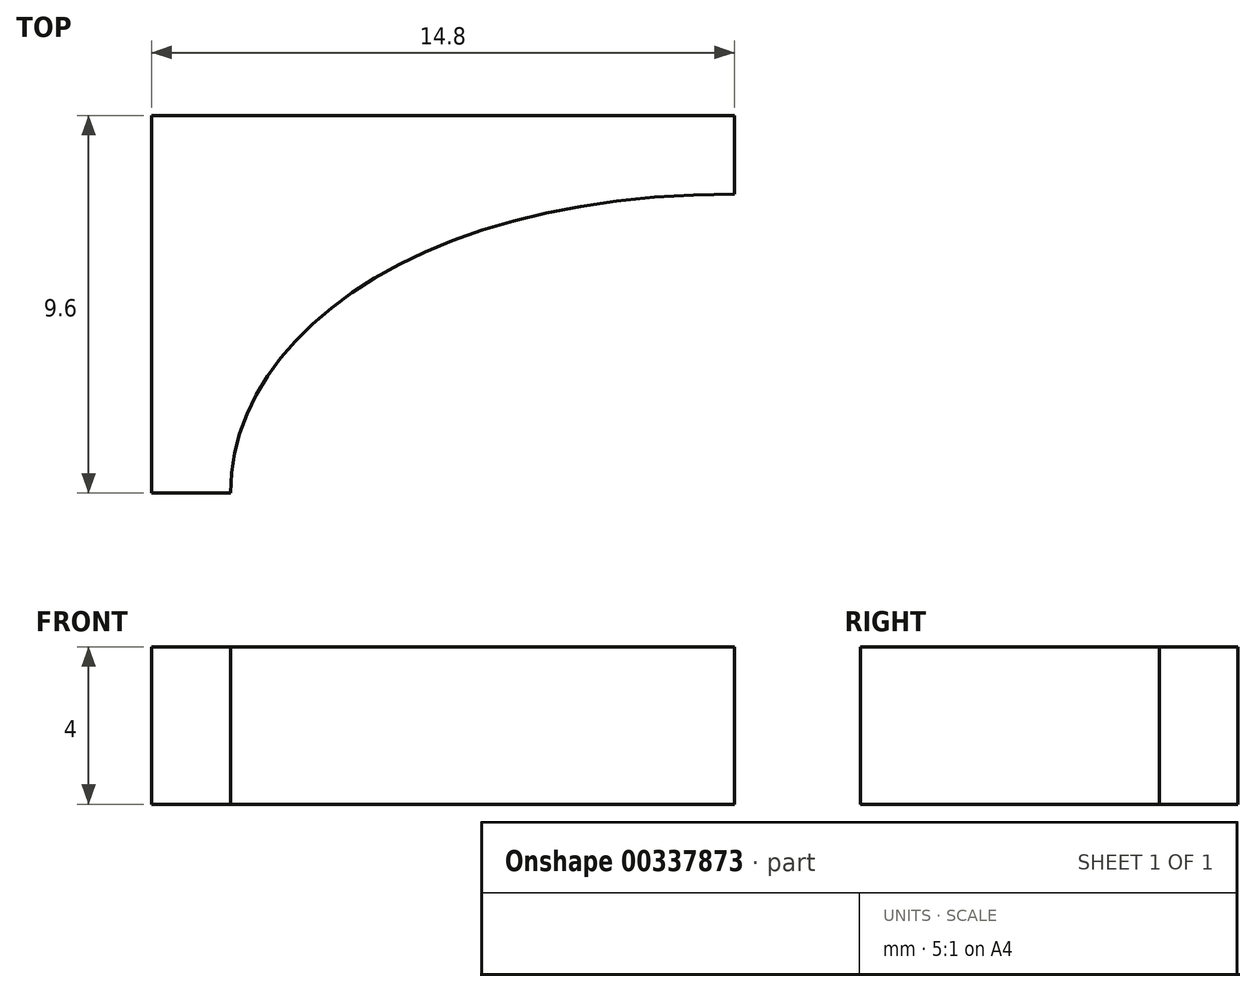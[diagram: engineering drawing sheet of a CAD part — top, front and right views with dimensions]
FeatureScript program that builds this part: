
annotation { "Feature Type Name" : "Feature", "Feature Type Description" : "" }
export const myFeature = defineFeature(function(context is Context, id is Id, definition is map)
    precondition{}
    {
        {
            var Q0;
            Q0=qCreatedBy(makeId("Top.planeOp"),FACE);
            var sketch = newSketch(context, id + "F0", { "sketchPlane" : qUnion([Q0])});
            skPoint(sketch, "E0.middle", {"position": v(0, 0) * mm});
            skFitSpline(sketch, "E1", {"points": [v(-12.8, 0) * mm, v(0, 7.6) * mm], "startDerivative": vector(0, 11.86) * mm, "endDerivative": vector(24.22, 0) * mm});
            skPoint(sketch, "E2.orphan", {"position": v(-12.8, 7.6) * mm});
            skPoint(sketch, "E0.bottom.end.orphan", {"position": v(-12.8, -7.6) * mm});
            skPoint(sketch, "E3.orphan", {"position": v(12.8, -7.6) * mm});
            skPoint(sketch, "E0.top.start.orphan", {"position": v(12.8, 7.6) * mm});
            skPoint(sketch, "E4.end.orphan", {"position": v(12.8, 0) * mm});
            skLineSegment(sketch, "E5", {"start": v(-12.8, 0) * mm, "end": v(-14.8, 0) * mm});
            skLineSegment(sketch, "E6", {"start": v(0, 7.6) * mm, "end": v(0, 9.6) * mm});
            skLineSegment(sketch, "E7", {"start": v(0, 9.6) * mm, "end": v(-14.8, 9.6) * mm});
            skLineSegment(sketch, "E8", {"start": v(-14.8, 0) * mm, "end": v(-14.8, 9.6) * mm});
            skSolve(sketch);
        }
        {
            var Q0;
            Q0 = qSketchRegion(id + "F0", true);
            extrude(context, id + "F1", {"entities" : qUnion([Q0]), "depth" : 4 * mm});
        }
    });
